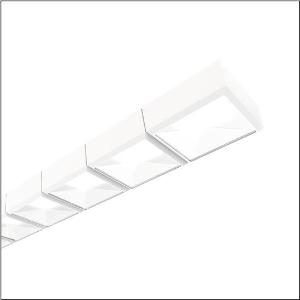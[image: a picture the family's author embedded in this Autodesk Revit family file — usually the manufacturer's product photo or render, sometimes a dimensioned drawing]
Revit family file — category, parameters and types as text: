
# Revit family: scriptus_r__11_5mz212d03wa_20e5
name_source: partatom
category: Lighting Fixtures
units: mm (PartAtom-declared; Revit-internal decimal feet)

## family parameters
Cut with Voids When Loaded = No
Host = Face
Light Source = No
Part Type = Normal
Room Calculation Point = No
Round Connector Dimension = Use Diameter
Shared = No

## types (1)
- Scriptus® 11 (1 x LED 3000K / CRI = 80 (unbekannt), 2200 lm, 3000K)
    Apparent Load = 35 VA
    CIE Flux Codes = 82 95 99 100 100
    Color Rendering = 80
    Color Temperature = 3000K
    Default Elevation = 1800 mm
    Description = Scriptus® 11, office luminaire, primary optical cover: lenses, CAT 2 (L<= 3000cd/m²), light emission: direct distribution, primary light characteristic: symmetric, installation type: surface-mounted, LED, rated luminous flux: 4.390lm, luminous efficacy: 127lm/W, light colour: 830, colour temperature: 3000K, control gear: ECG DALI, with terminal, 5-pole, mains connection: 230V, AC, 50Hz, rated input power: 35W, housing, luminaire housing, of aluminium, traffic white (RAL 9016), length: 1.658mm, width: 114mm, height: 57mm, protection rating (complete): IP20, insulation class (complete): insulation class I (protective earthing), certification: CE, ENEC, VDE, protection symbol: F, permissible operating ambient temperature: 0..+35°C, standard: EN 50419, packaging unit: 1 piece
    Height = 57 mm
    Lamp = 1 x LED 3000K / CRI >= 80 (unbekannt)
    Lamp Light Flux = 2200 lm
    Lamp count = 1
    Length = 1658 mm
    Luminous efficacy = 127 lm/W
    Manufacturer = Siteco
    ModVariant = No
    Model = 5MZ212D03WA
    Mounting Place = Ceiling
    Mounting Type = Surface mounted
    Number of Poles = 1
    OnlyDefault = Yes
    Power Factor = 1
    Product Name = Scriptus® 11
    Product group = office luminaire | ceiling mounted
    ProductGroupID = 304
    Protection Class = Protection class I
    Protection Degree = IP 20
    RLX_Detail_Level = 1
    RLX_Emergency_Light_Flux = 0 lm
    RLX_Emergency_Type = 0
    RLX_Emergency_Type_DB = No
    RlxData = <blob elided: 29505 chars, md5=446de893>
    Socket = socket
    Standby Power = 0 W
    System Light Flux = 4400 lm
    System Power = 35 W
    Type Comments = Product without accessories
    Type Image = l_1004833.jpg
    URL = http://relux.com
    VarID = ---
    Voltage = 0 V
    Weight = 0.00 kg
    Width = 114 mm

## geometry (parser evidence)
native form markers: Blend x4, Sweep x14
no freeform markers — native parametric forms only
